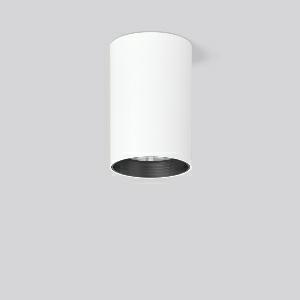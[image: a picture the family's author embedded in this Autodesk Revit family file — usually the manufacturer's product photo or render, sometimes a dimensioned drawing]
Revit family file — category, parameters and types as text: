
# Revit family: heledon_maxi_a_931242_002_76_3329
name_source: partatom
category: Lighting Fixtures
units: mm (PartAtom-declared; Revit-internal decimal feet)

## family parameters
Cut with Voids When Loaded = No
Host = Face
Light Source = No
Part Type = Normal
Room Calculation Point = No
Round Connector Dimension = Use Diameter
Shared = No

## types (1)
- HELEDON maxi A (1 x LED Modul 920 meat+, 1850 lm, 2000)
    Apparent Load = 33 VA
    Approval mark = CE
    CIE Flux Codes = 96 99 100 100 100
    Color Rendering = 90
    Color Temperature = 2000
    Default Elevation = 1800 mm
    Description = Series: HELEDON maxi
Cylindrical surface-mounted downlight. Housing: die-cast aluminium, powder-coated. Internal ceiling frame polycarbonate with bayonet mounting. Black plastic ring and recessed LED to prevent glare from the side. Optical assembly with lens made of plastic (polycarbonate) for the best homogeneous light distribution - can be changed without tools. Special LED for illumination of meat included. Suitable for Ceiling mounting. Easy installation with a separate ceiling frame with bayonet mounting and plug connection. Driver integrated. Connected via plug-in connector. High quality converter without flickering and stroboscopic effect. The following accessories can be mounted without use of tools: interchangeable lenses, decorative glasses, honeycomb louvre, clear and frosted diffusers, white interchangeable plastic ring. 
Colour: traffic white, matt (RAL 9016)
Diameter: 123 mm
Height: 183 mm
Lamp: LED
Socket: without socket
Colour temperature: meat +
System power: 33 W
Rated luminous flux: 1850 lm
Luminous efficiency: 56 lm/W
Control gear: Converter, dimmable, DALI
Protection class: I
Type of protection: IP 20
    Height = 183 mm
    Lamp = 1 x LED Modul 920 meat+
    Lamp Light Flux = 1850 lm
    Lamp count = 1
    Length = 123 mm
    Lifetime = 50000 h
    Luminous efficacy = 56 lm/W
    Manufacturer = RZB
    ModVariant = No
    Model = 931242.002.76
    Mounting Place = Ceiling
    Mounting Type = Surface mounted
    Number of Poles = 1
    OnlyDefault = Yes
    Power Factor = 1
    Product Name = HELEDON maxi A
    Product group = Surface mounted downlights
    ProductGroupID = 302
    Protection Class = Protection class I
    Protection Degree = IP 20
    RLX_Detail_Level = 1
    RLX_Emergency_Light_Flux = 0 lm
    RLX_Emergency_Type = 0
    RLX_Emergency_Type_DB = No
    RlxData = <blob elided: 99737 chars, md5=4fc569f3>
    Socket = socket
    Standby Power = 0 W
    System Light Flux = 1850 lm
    System Power = 33 W
    Type Comments = Product without accessories
    Type Image = 931193.002.jpg
    URL = http://relux.com
    VarID = ---
    Voltage = 230 V
    Voltage Range = 220-240 V
    Weight = 0.00 kg
    Width = 0 mm  [stored 0 ft]

note: [stored X ft] marks values corroborated as IEEE doubles in the binary element streams (Revit-internal decimal feet)

## geometry (parser evidence)
native form markers: Blend x4, Sweep x12
no freeform markers — native parametric forms only
